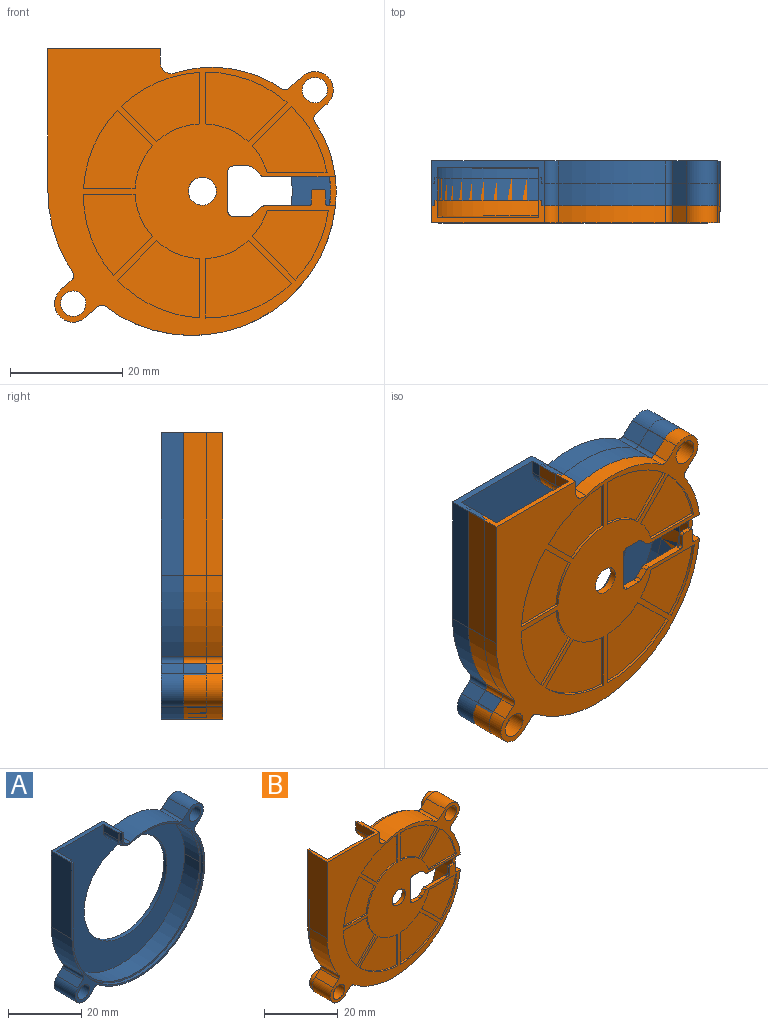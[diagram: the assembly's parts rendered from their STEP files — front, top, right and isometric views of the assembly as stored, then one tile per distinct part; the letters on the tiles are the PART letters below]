
ASSEMBLY  parts=2 mates=1
PART A: 35 faces, bbox 51.3x8x51.1 mm
  f0: cylinder r=25.15mm len=50.3mm, axis (0,-1,0), area 79mm2, adj f28,f32,f33,f34
  f1: cylinder r=2.5mm len=3.25mm, axis (0,-1,0), area 4.7mm2, adj f28,f31,f32,f34
  f2: cylinder r=2.25mm len=8mm, axis (0,1,0), area 113.1mm2, adj f28,f29
  f3: cylinder r=2.25mm len=8mm, axis (0,1,0), area 113.1mm2, adj f28,f29
  f4: cylinder r=22.07mm len=19.05mm, axis (0,1,0), area 159.4mm2, adj f20,f21,f28,f29
  f5: cylinder r=3.3mm len=8mm, axis (0,1,0), area 82.9mm2, adj f18,f19,f28,f29
  f6: cylinder r=1mm len=8mm, axis (0,1,0), area 11mm2, adj f14,f15,f28,f29
  f7: cylinder r=16mm len=32mm, axis (0,1,0), area 120.6mm2, adj f29,f30
  f8: cylinder r=24.65mm len=49.3mm, axis (0,-1,0), area 449.3mm2, adj f11,f12,f30,f34
  f9: cylinder r=3mm len=5.8mm, axis (0,-1,0), area 32.6mm2, adj f10,f11,f30,f34
  f10: plane 5.8x2.44mm, normal (-1,0,0), area 14.2mm2, adj f9,f23,f30,f34
  f11: cylinder r=21.07mm len=27.4mm, axis (0,-1,0), area 229.2mm2, adj f8,f9,f30,f34
  f12: plane 25.4x5.8mm, normal (1,0,0), area 147.3mm2, adj f8,f23,f30,f34
  f13: cylinder r=3.3mm len=8mm, axis (0,1,0), area 82.9mm2, adj f14,f27,f28,f29
  f14: plane 8x2.22mm, normal (0.66,0,-0.75), area 23.7mm2, adj f6,f13,f28,f29
  f15: cylinder r=25.65mm len=41.13mm, axis (0,1,0), area 455.4mm2, adj f6,f16,f28,f29
  f16: cylinder r=22.07mm len=12.41mm, axis (0,1,0), area 105.5mm2, adj f15,f17,f28,f29
  f17: cylinder r=1mm len=8mm, axis (0,1,0), area 11.6mm2, adj f16,f18,f28,f29
  f18: plane 8x2.04mm, normal (0.66,0,-0.75), area 21.8mm2, adj f5,f17,f28,f29
  f19: plane 8x2.44mm, normal (-0.66,0,0.75), area 26mm2, adj f5,f20,f28,f29
  f20: cylinder r=1mm len=8mm, axis (0,1,0), area 10.6mm2, adj f4,f19,f28,f29
  f21: cylinder r=2mm len=8mm, axis (0,1,0), area 30mm2, adj f4,f22,f28,f29
  f22: plane 8x2.44mm, normal (1,0,0), area 19.6mm2, adj f21,f23,f28,f29
  f23: plane 20x8mm, normal (0,0,1), area 36.6mm2, adj f10,f12,f22,f24,f28,f29,f30,f31
  f24: plane 25.4x8mm, normal (-1,0,0), area 203.2mm2, adj f23,f25,f28,f29
  f25: cylinder r=25.65mm len=14.47mm, axis (0,1,0), area 122.9mm2, adj f24,f26,f28,f29
  f26: cylinder r=1mm len=8mm, axis (0,1,0), area 11.6mm2, adj f25,f27,f28,f29
  f27: plane 8x1.98mm, normal (-0.66,0,0.75), area 21.1mm2, adj f13,f26,f28,f29
  f28: plane 51.3x51.07mm, normal (0,-1,0), area 126.8mm2, adj f0,f1,f2,f3,f4,f5,f6,f13
  f29: plane 51.3x51.07mm, normal (0,1,0), area 1370.5mm2, adj f2,f3,f4,f5,f6,f7,f13,f14
  f30: plane 50.07x49.3mm, normal (0,-1,0), area 1168mm2, adj f7,f8,f9,f10,f11,f12,f23
  f31: plane 2.44x1mm, normal (-1,0,0), area 2.4mm2, adj f1,f23,f28,f34
  f32: cylinder r=21.57mm len=28.05mm, axis (0,-1,0), area 40.5mm2, adj f0,f1,f28,f34
  f33: plane 25.4x1mm, normal (1,0,0), area 25.4mm2, adj f0,f23,f28,f34
  f34: plane 50.57x50.3mm, normal (0,-1,0), area 75.6mm2, adj f0,f1,f8,f9,f10,f11,f12,f23
PART B: 104 faces, bbox 52.9x8.5x51.4 mm
  f0: torus R=1.41mm, axis (0,-1,0), area 1.6mm2, adj f31,f35,f102,f103
  f1: cylinder r=21.88mm len=15.3mm, axis (0,-1,0), area 8.4mm2, adj f14,f53,f54,f55
  f2: cylinder r=2.82mm len=5.65mm, axis (0,-1,0), area 26.6mm2, adj f15,f41
  f3: cylinder r=2.82mm len=5.65mm, axis (0,-1,0), area 26.6mm2, adj f15,f40
  f4: cylinder r=21.57mm len=28.05mm, axis (0,1,0), area 40.5mm2, adj f15,f16,f37,f38
  f5: cylinder r=21.07mm len=27.4mm, axis (0,1,0), area 266.7mm2, adj f16,f31,f33,f34,f86,f87
  f6: cylinder r=2.5mm len=5mm, axis (0,-1,0), area 18.8mm2, adj f14,f31
  f7: cylinder r=2.25mm len=8.5mm, axis (0,-1,0), area 120.2mm2, adj f14,f40
  f8: cylinder r=2.25mm len=8.5mm, axis (0,-1,0), area 120.2mm2, adj f14,f41
  f9: cylinder r=25.65mm len=41.13mm, axis (0,-1,0), area 393.3mm2, adj f13,f14,f15,f28,f29,f87
  f10: cylinder r=1mm len=7mm, axis (0,-1,0), area 9.3mm2, adj f14,f15,f23,f24
  f11: cylinder r=2mm len=7mm, axis (0,-1,0), area 26.3mm2, adj f14,f15,f22,f23
  f12: cylinder r=3.3mm len=7mm, axis (0,-1,0), area 72.6mm2, adj f14,f15,f17,f30
  f13: plane 12.66x2mm, normal (0,0,1), area 13.2mm2, adj f9,f14,f31,f34,f87,f93,f95,f98
  f14: plane 51.17x51.07mm, normal (0,-1,0), area 1131.7mm2, adj f1,f6,f7,f8,f9,f10,f11,f12
  f15: plane 51.3x51.07mm, normal (0,1,0), area 108.5mm2, adj f2,f3,f4,f9,f10,f11,f12,f17
  f16: plane 50.57x50.3mm, normal (0,1,0), area 75.6mm2, adj f4,f5,f21,f32,f33,f34,f35,f36
  f17: plane 7x1.98mm, normal (-0.66,0,0.75), area 18.5mm2, adj f12,f14,f15,f18
  f18: cylinder r=1mm len=7mm, axis (0,-1,0), area 10.1mm2, adj f14,f15,f17,f19
  f19: cylinder r=25.65mm len=14.47mm, axis (0,-1,0), area 107.6mm2, adj f14,f15,f18,f20
  f20: plane 25.4x7mm, normal (-1,0,0), area 177.8mm2, adj f14,f15,f19,f21
  f21: plane 20x8mm, normal (0,0,1), area 31.2mm2, adj f14,f15,f16,f20,f22,f32,f35,f36
  f22: plane 7x2.44mm, normal (1,0,0), area 17.1mm2, adj f11,f14,f15,f21
  f23: cylinder r=22.07mm len=19.05mm, axis (0,-1,0), area 139.5mm2, adj f10,f11,f14,f15
  f24: plane 7x2.44mm, normal (-0.66,0,0.75), area 22.8mm2, adj f10,f14,f15,f25
  f25: cylinder r=3.3mm len=7mm, axis (0,-1,0), area 72.6mm2, adj f14,f15,f24,f26
  f26: plane 7x2.04mm, normal (0.66,0,-0.75), area 19.1mm2, adj f14,f15,f25,f27
  f27: cylinder r=1mm len=7mm, axis (0,-1,0), area 10.1mm2, adj f14,f15,f26,f28
  f28: cylinder r=22.07mm len=12.41mm, axis (0,-1,0), area 87.1mm2, adj f9,f14,f15,f27,f86,f87
  f29: cylinder r=1mm len=7mm, axis (0,-1,0), area 9.6mm2, adj f9,f14,f15,f30
  f30: plane 7x2.22mm, normal (0.66,0,-0.75), area 20.7mm2, adj f12,f14,f15,f29
  f31: plane 49.16x46.35mm, normal (0,1,0), area 1650.7mm2, adj f0,f5,f6,f13,f33,f34,f35,f81
  f32: plane 7.1x2.44mm, normal (-1,0,0), area 17.4mm2, adj f16,f21,f33,f102
  f33: cylinder r=3mm len=7.1mm, axis (0,1,0), area 38.5mm2, adj f5,f16,f31,f32,f103
  f34: cylinder r=24.65mm len=49.3mm, axis (0,1,0), area 524.7mm2, adj f5,f13,f16,f31,f35,f87
  f35: plane 25.4x7.1mm, normal (1,0,0), area 179.6mm2, adj f0,f16,f21,f31,f34,f102
  f36: plane 25.4x1mm, normal (-1,0,0), area 25.4mm2, adj f15,f16,f21,f37
  f37: cylinder r=25.15mm len=50.3mm, axis (0,1,0), area 79mm2, adj f4,f15,f16,f36
  f38: cylinder r=2.5mm len=3.25mm, axis (0,1,0), area 4.7mm2, adj f4,f15,f16,f39
  f39: plane 2.44x1mm, normal (1,0,0), area 2.4mm2, adj f15,f16,f21,f38
  f40: plane 5.65x5.65mm, normal (0,1,0), area 9.2mm2, adj f3,f7
  f41: plane 5.65x5.65mm, normal (0,1,0), area 9.2mm2, adj f2,f8
  f42: plane 6.99x6.99mm, normal (0.71,0,-0.71), area 4.9mm2, adj f14,f43,f45,f46
  f43: cylinder r=12mm len=7.62mm, axis (0,-1,0), area 4.2mm2, adj f14,f42,f44,f46
  f44: plane 10.54x0.5mm, normal (-1,0,0), area 5.3mm2, adj f14,f43,f45,f46
  f45: cylinder r=21.88mm len=14.61mm, axis (0,-1,0), area 8.2mm2, adj f14,f42,f44,f46
  f46: plane 14.61x13.7mm, normal (0,-1,0), area 127.2mm2, adj f42,f43,f44,f45
  f47: plane 7.67x7.67mm, normal (0.71,0,0.71), area 5.4mm2, adj f14,f48,f50,f51
  f48: cylinder r=12mm len=4.77mm, axis (0,-1,0), area 2.8mm2, adj f14,f47,f49,f51
  f49: plane 10.88x0.5mm, normal (0,0,-1), area 5.4mm2, adj f14,f48,f50,f51
  f50: cylinder r=21.88mm len=12.45mm, axis (0,-1,0), area 7mm2, adj f14,f47,f49,f51
  f51: plane 13.57x12.45mm, normal (0,-1,0), area 105.4mm2, adj f47,f48,f49,f50
  f52: cylinder r=12mm len=7.62mm, axis (0,-1,0), area 4.2mm2, adj f14,f53,f54,f55
  f53: plane 7.67x7.67mm, normal (-0.71,0,-0.71), area 5.4mm2, adj f1,f14,f52,f55
  f54: plane 10.57x0.5mm, normal (1,0,0), area 5.3mm2, adj f1,f14,f52,f55
  f55: plane 15.3x13.73mm, normal (0,-1,0), area 135.9mm2, adj f1,f52,f53,f54
  f56: cylinder r=12mm len=7.62mm, axis (0,-1,0), area 4.2mm2, adj f14,f57,f59,f60
  f57: plane 9.2x0.5mm, normal (1,0,0), area 4.6mm2, adj f14,f56,f58,f60
  f58: cylinder r=21.88mm len=14.58mm, axis (0,-1,0), area 7.9mm2, adj f14,f57,f59,f60
  f59: plane 6.96x6.96mm, normal (-0.71,0,0.71), area 4.9mm2, adj f14,f56,f58,f60
  f60: plane 14.58x12.36mm, normal (0,-1,0), area 115.4mm2, adj f56,f57,f58,f59
  f61: cylinder r=12mm len=4.77mm, axis (0,-1,0), area 2.8mm2, adj f14,f62,f64,f65
  f62: plane 6.99x6.99mm, normal (0.71,0,-0.71), area 4.9mm2, adj f14,f61,f63,f65
  f63: cylinder r=21.88mm len=11.76mm, axis (0,-1,0), area 6.8mm2, adj f14,f62,f64,f65
  f64: plane 10.66x0.5mm, normal (0,0,1), area 5.3mm2, adj f14,f61,f63,f65
  f65: plane 13.36x11.76mm, normal (0,-1,0), area 97mm2, adj f61,f62,f63,f64
  f66: cylinder r=12mm len=7.62mm, axis (0,-1,0), area 4.2mm2, adj f14,f67,f69,f70
  f67: plane 9.17x0.5mm, normal (0,0,1), area 4.6mm2, adj f14,f66,f68,f70
  f68: cylinder r=21.88mm len=13.93mm, axis (0,-1,0), area 7.7mm2, adj f14,f67,f69,f70
  f69: plane 6.3x6.3mm, normal (-0.71,0,-0.71), area 4.5mm2, adj f14,f66,f68,f70
  f70: plane 13.93x12.33mm, normal (0,-1,0), area 107.6mm2, adj f66,f67,f68,f69
  f71: plane 9.17x0.5mm, normal (-1,0,0), area 4.6mm2, adj f14,f72,f74,f75
  f72: cylinder r=12mm len=7.62mm, axis (0,-1,0), area 4.2mm2, adj f14,f71,f73,f75
  f73: plane 6.3x6.3mm, normal (0.71,0,0.71), area 4.5mm2, adj f14,f72,f74,f75
  f74: cylinder r=21.88mm len=13.93mm, axis (0,-1,0), area 7.7mm2, adj f14,f71,f73,f75
  f75: plane 13.93x12.33mm, normal (0,-1,0), area 107.6mm2, adj f71,f72,f73,f74
  f76: cylinder r=12mm len=7.62mm, axis (0,-1,0), area 4.2mm2, adj f14,f77,f79,f80
  f77: plane 6.96x6.96mm, normal (-0.71,0,0.71), area 4.9mm2, adj f14,f76,f78,f80
  f78: cylinder r=21.88mm len=14.58mm, axis (0,-1,0), area 7.9mm2, adj f14,f77,f79,f80
  f79: plane 9.2x0.5mm, normal (0,0,-1), area 4.6mm2, adj f14,f76,f78,f80
  f80: plane 14.58x12.36mm, normal (0,-1,0), area 115.4mm2, adj f76,f77,f78,f79
  f81: plane 1.31x1.31mm, normal (-0.71,0,0.71), area 2.2mm2, adj f14,f31,f92,f93
  f82: plane 2.79x1.2mm, normal (0,0,1), area 3.3mm2, adj f14,f31,f91,f92
  f83: plane 7x1.2mm, normal (1,0,0), area 8.4mm2, adj f14,f31,f88,f91
  f84: plane 2.79x1.2mm, normal (0,0,-1), area 3.3mm2, adj f14,f31,f88,f90
  f85: plane 1.31x1.31mm, normal (-0.71,0,-0.71), area 2.2mm2, adj f14,f31,f89,f90
  f86: plane 12.63x2mm, normal (0,0,-1), area 16mm2, adj f5,f14,f28,f31,f87,f89
  f87: plane 5.2x1.16mm, normal (0,-1,0), area 5.2mm2, adj f5,f9,f13,f28,f34,f86
  f88: cylinder r=1mm len=1.2mm, axis (0,1,0), area 1.9mm2, adj f14,f31,f83,f84
  f89: cylinder r=1mm len=1.2mm, axis (0,-1,0), area 0.9mm2, adj f14,f31,f85,f86
  f90: cylinder r=1mm len=1.2mm, axis (0,1,0), area 0.9mm2, adj f14,f31,f84,f85
  f91: cylinder r=1mm len=1.2mm, axis (0,1,0), area 1.9mm2, adj f14,f31,f82,f83
  f92: cylinder r=1mm len=1.2mm, axis (0,1,0), area 0.9mm2, adj f14,f31,f81,f82
  f93: cylinder r=1mm len=1.2mm, axis (0,-1,0), area 0.9mm2, adj f13,f14,f31,f81
  f94: plane 2x0.8mm, normal (1,0,0), area 1.6mm2, adj f14,f95,f100,f101
  f95: plane 3.5x3mm, normal (0,1,0), area 7.5mm2, adj f13,f94,f96,f97,f98,f99,f100,f101
  f96: plane 2x0.8mm, normal (-1,0,0), area 1.6mm2, adj f14,f95,f98,f99
  f97: plane 1.5x0.8mm, normal (0,0,1), area 1.2mm2, adj f14,f95,f99,f100
  f98: cylinder r=0.5mm len=0.8mm, axis (0,1,0), area 0.6mm2, adj f13,f14,f95,f96
  f99: cylinder r=0.5mm len=0.8mm, axis (0,1,0), area 0.6mm2, adj f14,f95,f96,f97
  f100: cylinder r=0.5mm len=0.8mm, axis (0,-1,0), area 0.6mm2, adj f14,f94,f95,f97
  f101: cylinder r=0.5mm len=0.8mm, axis (0,-1,0), area 0.6mm2, adj f13,f14,f94,f95
  f102: plane 22.44x18mm, normal (0,1,0), area 150.3mm2, adj f0,f21,f32,f35,f103
  f103: torus R=22.35mm, axis (0,1,0), area 37.3mm2, adj f0,f31,f33,f102
PLACE A t=(-9.02,17.05,-3.2)mm
PLACE B t=(-9.02,6.05,-3.2)mm
MATE fastened B.f3 <-> A.f2  axis (0,1,0) through (10.98,13.05,14.8)mm
